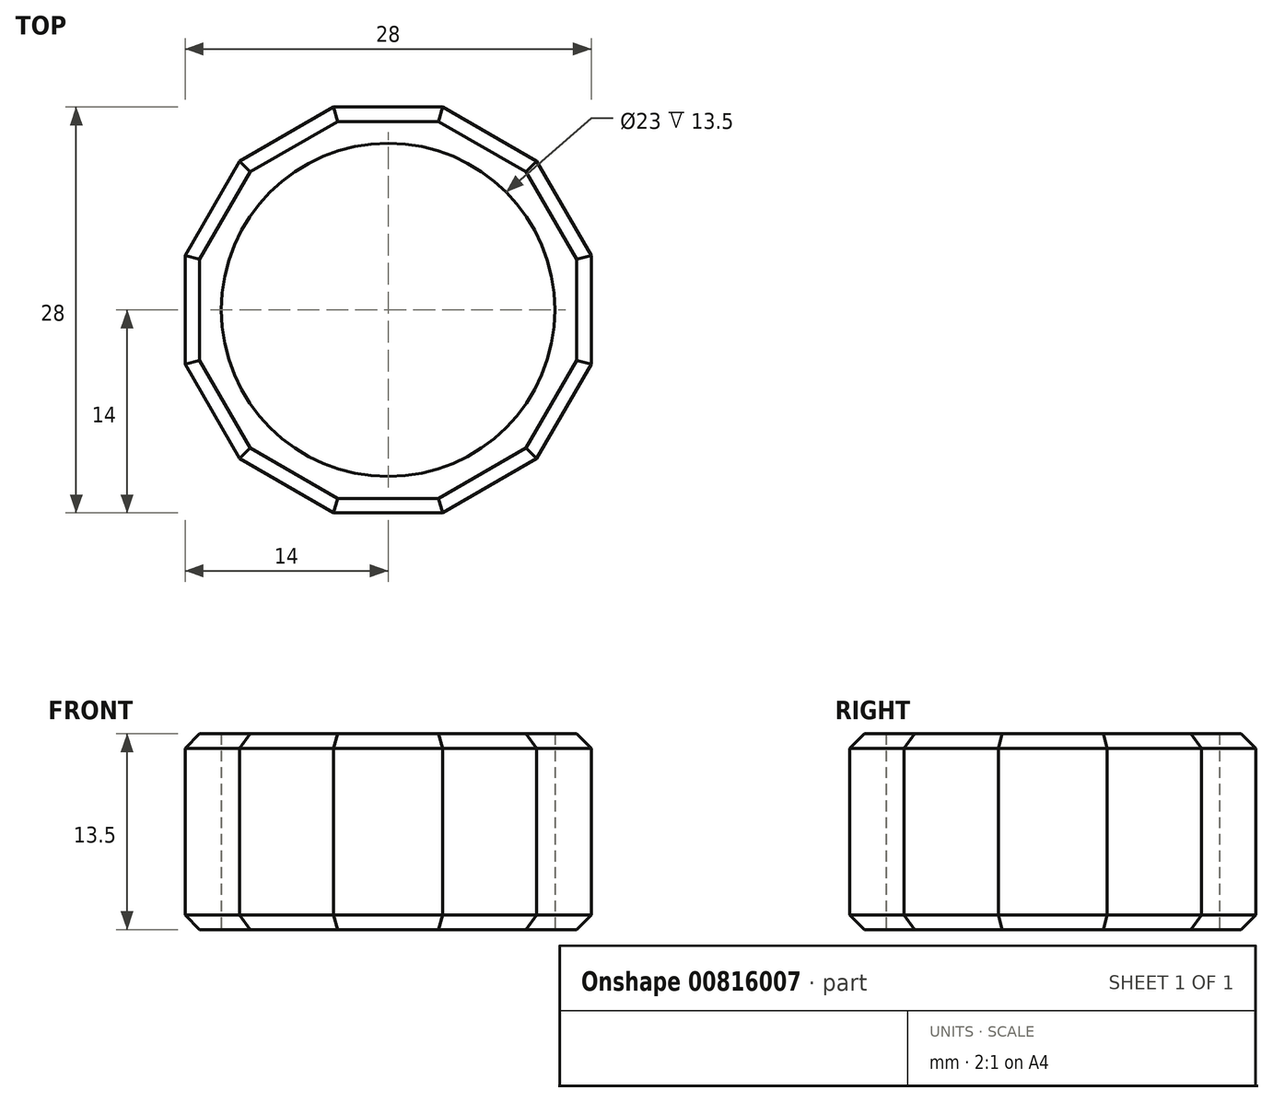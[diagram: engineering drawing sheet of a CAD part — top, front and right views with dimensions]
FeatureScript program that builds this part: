
annotation { "Feature Type Name" : "Feature", "Feature Type Description" : "" }
export const myFeature = defineFeature(function(context is Context, id is Id, definition is map)
    precondition{}
    {
        {
            var Q0;
            Q0=qCreatedBy(makeId("Top.planeOp"),FACE);
            var sketch = newSketch(context, id + "F0", { "sketchPlane" : qUnion([Q0])});
            skCircle(sketch, "E0", {"center": v(0, 0) * mm, "radius": 11.5 * mm});
            skCircle(sketch, "E1.cCircle", {"center": v(0, 0) * mm, "radius": 14 * mm, "construction": true});
            skLineSegment(sketch, "E1.0", {"start": v(14, 3.75) * mm, "end": v(14, -3.75) * mm});
            skLineSegment(sketch, "E1.1", {"start": v(14, -3.75) * mm, "end": v(10.25, -10.25) * mm});
            skLineSegment(sketch, "E1.2", {"start": v(10.25, -10.25) * mm, "end": v(3.75, -14) * mm});
            skLineSegment(sketch, "E1.3", {"start": v(3.75, -14) * mm, "end": v(-3.75, -14) * mm});
            skLineSegment(sketch, "E1.4", {"start": v(-3.75, -14) * mm, "end": v(-10.25, -10.25) * mm});
            skLineSegment(sketch, "E1.5", {"start": v(-10.25, -10.25) * mm, "end": v(-14, -3.75) * mm});
            skLineSegment(sketch, "E1.6", {"start": v(-14, -3.75) * mm, "end": v(-14, 3.75) * mm});
            skLineSegment(sketch, "E1.7", {"start": v(-14, 3.75) * mm, "end": v(-10.25, 10.25) * mm});
            skLineSegment(sketch, "E1.8", {"start": v(-10.25, 10.25) * mm, "end": v(-3.75, 14) * mm});
            skLineSegment(sketch, "E1.9", {"start": v(-3.75, 14) * mm, "end": v(3.75, 14) * mm});
            skLineSegment(sketch, "E1.10", {"start": v(3.75, 14) * mm, "end": v(10.25, 10.25) * mm});
            skLineSegment(sketch, "E1.11", {"start": v(10.25, 10.25) * mm, "end": v(14, 3.75) * mm});
            skPoint(sketch, "E1.0.midPoint", {"position": v(14, 0) * mm});
            skSolve(sketch);
        }
        {
            var Q0;
            Q0=makeQuery(id+"F0.imprint","IMPRINT",FACE,{"disambiguationData":[TD([[makeQuery(id+"F0.imprint","IMPRINT",EDGE,{"derivedFrom":sQuery(id+"F0.wireOp",EDGE,"E0")}),-1.0]])]});
            extrude(context, id + "F1", {"entities" : qUnion([Q0]), "depth" : 13.5 * mm, "offsetDistance" : 25 * mm});
        }
        {
            var Q0;
            Q0=makeQuery(id+"F1.opExtrude","CAP_EDGE",EDGE,{"disambiguationData":[OSD([sQuery(id+"F0.wireOp",EDGE,"E1.2")])],"isStart":false});
            var Q1;
            Q1=makeQuery(id+"F1.opExtrude","CAP_EDGE",EDGE,{"disambiguationData":[OSD([sQuery(id+"F0.wireOp",EDGE,"E1.0")])],"isStart":false});
            var Q2;
            Q2=makeQuery(id+"F1.opExtrude","CAP_EDGE",EDGE,{"disambiguationData":[OSD([sQuery(id+"F0.wireOp",EDGE,"E1.11")])],"isStart":false});
            var Q3;
            Q3=makeQuery(id+"F1.opExtrude","CAP_EDGE",EDGE,{"disambiguationData":[OSD([sQuery(id+"F0.wireOp",EDGE,"E1.10")])],"isStart":false});
            var Q4;
            Q4=makeQuery(id+"F1.opExtrude","CAP_EDGE",EDGE,{"disambiguationData":[OSD([sQuery(id+"F0.wireOp",EDGE,"E1.9")])],"isStart":false});
            var Q5;
            Q5=makeQuery(id+"F1.opExtrude","CAP_EDGE",EDGE,{"disambiguationData":[OSD([sQuery(id+"F0.wireOp",EDGE,"E1.8")])],"isStart":false});
            var Q6;
            Q6=makeQuery(id+"F1.opExtrude","CAP_EDGE",EDGE,{"disambiguationData":[OSD([sQuery(id+"F0.wireOp",EDGE,"E1.7")])],"isStart":false});
            var Q7;
            Q7=makeQuery(id+"F1.opExtrude","CAP_EDGE",EDGE,{"disambiguationData":[OSD([sQuery(id+"F0.wireOp",EDGE,"E1.6")])],"isStart":false});
            var Q8;
            Q8=makeQuery(id+"F1.opExtrude","CAP_EDGE",EDGE,{"disambiguationData":[OSD([sQuery(id+"F0.wireOp",EDGE,"E1.5")])],"isStart":false});
            var Q9;
            Q9=makeQuery(id+"F1.opExtrude","CAP_EDGE",EDGE,{"disambiguationData":[OSD([sQuery(id+"F0.wireOp",EDGE,"E1.4")])],"isStart":false});
            var Q10;
            Q10=makeQuery(id+"F1.opExtrude","CAP_EDGE",EDGE,{"disambiguationData":[OSD([sQuery(id+"F0.wireOp",EDGE,"E1.3")])],"isStart":false});
            var Q11;
            Q11=makeQuery(id+"F1.opExtrude","CAP_EDGE",EDGE,{"disambiguationData":[OSD([sQuery(id+"F0.wireOp",EDGE,"E1.0")])],"isStart":true});
            var Q12;
            Q12=makeQuery(id+"F1.opExtrude","CAP_EDGE",EDGE,{"disambiguationData":[OSD([sQuery(id+"F0.wireOp",EDGE,"E1.11")])],"isStart":true});
            var Q13;
            Q13=makeQuery(id+"F1.opExtrude","CAP_EDGE",EDGE,{"disambiguationData":[OSD([sQuery(id+"F0.wireOp",EDGE,"E1.10")])],"isStart":true});
            var Q14;
            Q14=makeQuery(id+"F1.opExtrude","CAP_EDGE",EDGE,{"disambiguationData":[OSD([sQuery(id+"F0.wireOp",EDGE,"E1.9")])],"isStart":true});
            var Q15;
            Q15=makeQuery(id+"F1.opExtrude","CAP_EDGE",EDGE,{"disambiguationData":[OSD([sQuery(id+"F0.wireOp",EDGE,"E1.8")])],"isStart":true});
            var Q16;
            Q16=makeQuery(id+"F1.opExtrude","CAP_EDGE",EDGE,{"disambiguationData":[OSD([sQuery(id+"F0.wireOp",EDGE,"E1.7")])],"isStart":true});
            var Q17;
            Q17=makeQuery(id+"F1.opExtrude","CAP_EDGE",EDGE,{"disambiguationData":[OSD([sQuery(id+"F0.wireOp",EDGE,"E1.6")])],"isStart":true});
            var Q18;
            Q18=makeQuery(id+"F1.opExtrude","CAP_EDGE",EDGE,{"disambiguationData":[OSD([sQuery(id+"F0.wireOp",EDGE,"E1.5")])],"isStart":true});
            var Q19;
            Q19=makeQuery(id+"F1.opExtrude","CAP_EDGE",EDGE,{"disambiguationData":[OSD([sQuery(id+"F0.wireOp",EDGE,"E1.4")])],"isStart":true});
            var Q20;
            Q20=makeQuery(id+"F1.opExtrude","CAP_EDGE",EDGE,{"disambiguationData":[OSD([sQuery(id+"F0.wireOp",EDGE,"E1.3")])],"isStart":true});
            var Q21;
            Q21=makeQuery(id+"F1.opExtrude","CAP_EDGE",EDGE,{"disambiguationData":[OSD([sQuery(id+"F0.wireOp",EDGE,"E1.2")])],"isStart":true});
            var Q22;
            Q22=makeQuery(id+"F1.opExtrude","CAP_EDGE",EDGE,{"disambiguationData":[OSD([sQuery(id+"F0.wireOp",EDGE,"E1.1")])],"isStart":true});
            var Q23;
            Q23=makeQuery(id+"F1.opExtrude","CAP_EDGE",EDGE,{"disambiguationData":[OSD([sQuery(id+"F0.wireOp",EDGE,"E1.1")])],"isStart":false});
            chamfer(context, id + "F2", {"entities" : qUnion([Q0, Q1, Q2, Q3, Q4, Q5, Q6, Q7, Q8, Q9, Q10, Q11, Q12, Q13, Q14, Q15, Q16, Q17, Q18, Q19, Q20, Q21, Q22, Q23]), "width" : 1 * mm, "tangentPropagation" : true});
        }
    });
